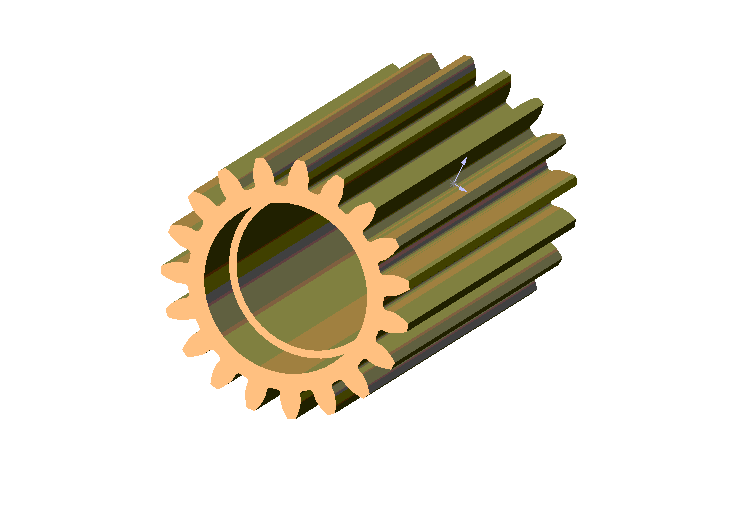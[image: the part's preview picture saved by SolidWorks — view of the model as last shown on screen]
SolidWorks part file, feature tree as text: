
SOLIDWORKS PART (.sldprt)
format: sldprt  version: not decoded by parser v0  size: 367,616 bytes
history: native  units: mm
features: sketch x21, plane x4, cut_extrude x3, material x1, fillet x1, pattern_circular x1 (+8 scaffold rows collapsed)
feature tree (39):
  scaffold x8  (default folders/planes/origin — collapsed)
  material  "Matériau <non spécifié>"
  plane  "Plane1"
  plane  "Plane2"
  plane  "Plane3"
  sketch  "Esquisse1"  dims[c1.D2=7.6mm c1.D1=42.0mm c2.D1=~9.473684deg]
  sketch  "Esquisse2"  dims[c1.D2=~7.447221mm c1.D1=37.0mm c2.D1=~10.243359deg]
  sketch  "Esquisse3"  dims[c1.D2=~7.294443mm c1.D1=33.0mm c2.D1=~10.846766deg]
  sketch  "Esquisse4"  dims[c1.D2=~7.141664mm c1.D1=30.0mm c2.D1=~11.181601deg]
  sketch  "Esquisse5"  dims[c1.D2=~7.866667mm c1.D1=46.0mm c2.D1=~7.836433deg]
  sketch  "Esquisse6"  dims[c1.D2=~8.133333mm c1.D1=50.0mm c2.D1=~5.91069deg]
  sketch  "Esquisse7"  dims[c1.D2=8.4mm c1.D1=54.0mm c2.D1=~3.757333deg]
  plane  "Plan1"  Offset=27mm
  sketch  "Esquisse8"  dims[c1.D2=7.6mm c1.D1=18.0mm c2.D1=~9.473684deg]
  sketch  "Esquisse9"  dims[c1.D2=~7.447221mm c1.D1=15.0mm c2.D1=~10.243359deg]
  sketch  "Esquisse10"  dims[c1.D2=~7.294443mm c1.D1=13.0mm c2.D1=~10.846766deg]
  sketch  "Esquisse11"  dims[c1.D2=~7.141664mm c1.D1=12.0mm c2.D1=~11.181601deg]
  sketch  "Esquisse12"  dims[c1.D2=~7.866667mm c1.D1=20.0mm c2.D1=~7.836433deg]
  sketch  "Esquisse13"  dims[c1.D2=~8.133333mm c1.D1=21.0mm c2.D1=~5.91069deg]
  sketch  "Esquisse14"  dims[c1.D2=8.4mm c1.D1=22.0mm c2.D1=~3.757333deg]
  sketch  "Esquisse15"  dims[c1.D2=6.6mm c1.D1=23.0mm c2.D1=~11.181601deg]
  sketch  "Esquisse16"  dims[c1.D2=6.6mm c1.D1=10.0mm c2.D1=~11.181601deg]
  sketch  "Esquisse17"  dims[D1=13.2mm]
  sketch  "Esquisse18"  dims[D1=13.2mm]
  fillet  "Congé1"  Radius=0.25mm
  pattern_circular  "Répétition circulaire1"  Count=19 Angle=360deg
  sketch  "Esquisse19"  dims[D1=10.0mm]
  cut_extrude  "Enlèv. mat.-Extru.1"  [1 undecoded]
  sketch  "Esquisse20"  dims[D1=11.0mm]
  cut_extrude  "Enlèv. mat.-Extru.2"  Depth=4mm
  sketch  "Esquisse22"  dims[D1=11.0mm]
  cut_extrude  "Enlèv. mat.-Extru.4"  Depth=1mm
decode coverage: 25 of 26 modeling features carry decoded parameters
note: ~ marks probable driven/reference dimensions
note: 1 parameter value undecoded
note: suppression state not decoded; provenance and decode notes live in map.json
